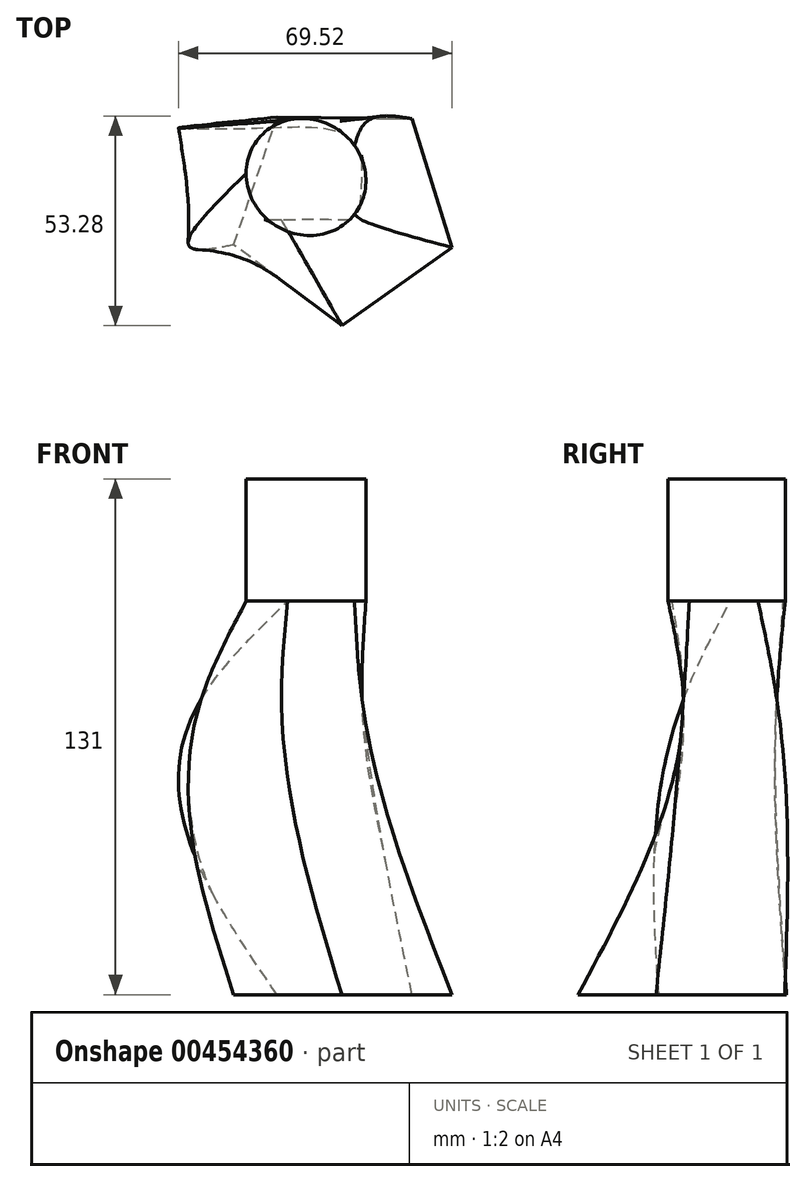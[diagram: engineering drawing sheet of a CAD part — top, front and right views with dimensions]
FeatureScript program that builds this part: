
annotation { "Feature Type Name" : "Feature", "Feature Type Description" : "" }
export const myFeature = defineFeature(function(context is Context, id is Id, definition is map)
    precondition{}
    {
        {
            var Q0;
            Q0=qCreatedBy(makeId("Top.planeOp"),FACE);
            var sketch = newSketch(context, id + "F0", { "sketchPlane" : qUnion([Q0])});
            skCircle(sketch, "E0.cCircle", {"center": v(0, 0) * mm, "radius": 23.6 * mm, "construction": true});
            skLineSegment(sketch, "E0.0", {"start": v(27.62, -9.36) * mm, "end": v(-0.36, -29.16) * mm});
            skLineSegment(sketch, "E0.1", {"start": v(-0.36, -29.16) * mm, "end": v(-27.85, -8.67) * mm});
            skLineSegment(sketch, "E0.2", {"start": v(-27.85, -8.67) * mm, "end": v(-16.85, 23.8) * mm});
            skLineSegment(sketch, "E0.3", {"start": v(-16.85, 23.8) * mm, "end": v(17.44, 23.38) * mm});
            skLineSegment(sketch, "E0.4", {"start": v(17.44, 23.38) * mm, "end": v(27.62, -9.36) * mm});
            skPoint(sketch, "E0.0.midPoint", {"position": v(13.63, -19.26) * mm});
            skSolve(sketch);
        }
        {
            var Q0;
            Q0=qCreatedBy(makeId("Top.planeOp"),FACE);
            cPlane(context, id + "F1", {"entities" : qUnion([Q0]), "cplaneType" : CPlaneType.OFFSET, "offset" : 75 * mm, "width" : 150 * mm, "height" : 150 * mm});
        }
        {
            var Q0;
            Q0=qCreatedBy(id+"F1.planeOp",FACE);
            var sketch = newSketch(context, id + "F2", { "sketchPlane" : qUnion([Q0])});
            skLineSegment(sketch, "E1.bottom", {"start": v(4.74, -2.37) * mm, "end": v(-36.15, -2.37) * mm});
            skLineSegment(sketch, "E1.top", {"start": v(4.74, 21.33) * mm, "end": v(-36.15, 21.33) * mm});
            skLineSegment(sketch, "E1.left", {"start": v(4.74, -2.37) * mm, "end": v(4.74, 21.33) * mm});
            skLineSegment(sketch, "E1.right", {"start": v(-36.15, -2.37) * mm, "end": v(-36.15, 21.33) * mm});
            skPoint(sketch, "E1.middle", {"position": v(-15.7, 9.48) * mm});
            skSolve(sketch);
        }
        {
            var Q0;
            Q0=qCreatedBy(id+"F1.planeOp",FACE);
            cPlane(context, id + "F3", {"entities" : qUnion([Q0]), "cplaneType" : CPlaneType.OFFSET, "offset" : 25 * mm, "width" : 150 * mm, "height" : 150 * mm});
        }
        {
            var Q0;
            Q0=qCreatedBy(id+"F3.planeOp",FACE);
            var sketch = newSketch(context, id + "F4", { "sketchPlane" : qUnion([Q0])});
            skEllipse(sketch, "E2", {"center": v(-9.48, 8.6) * mm, "majorRadius": 15.54 * mm, "minorRadius": 14.55 * mm, "majorAxis": v(0.82, -0.57)});
            skSolve(sketch);
        }
        {
            var Q0;
            Q0=makeQuery(id+"F0.imprint","IMPRINT",FACE,{"disambiguationData":[TD([[makeQuery(id+"F0.imprint","IMPRINT",EDGE,{"derivedFrom":sQuery(id+"F0.wireOp",EDGE,"E0.0")}),-1.0]])]});
            var Q1;
            Q1=makeQuery(id+"F2.imprint","IMPRINT",FACE,{"disambiguationData":[TD([[makeQuery(id+"F2.imprint","IMPRINT",EDGE,{"derivedFrom":sQuery(id+"F2.wireOp",EDGE,"E1.bottom")}),-1.0]])]});
            var Q2;
            Q2=makeQuery(id+"F4.imprint","IMPRINT",FACE,{"disambiguationData":[TD([[makeQuery(id+"F4.imprint","IMPRINT",EDGE,{"derivedFrom":sQuery(id+"F4.wireOp",EDGE,"E2")}),1.0]])]});
            loft(context, id + "F5", {"sheetProfilesArray" : [{ "sheetProfileEntities" : qUnion([Q0]) }, { "sheetProfileEntities" : qUnion([Q1]) }, { "sheetProfileEntities" : qUnion([Q2]) }]});
        }
        {
            var Q0;
            Q0=makeQuery(id+"F5.opLoft","CAP_FACE",FACE,{"disambiguationData":[OSD([makeQuery(id+"F4.imprint","IMPRINT",FACE,{"disambiguationData":[TD([[makeQuery(id+"F4.imprint","IMPRINT",EDGE,{"derivedFrom":sQuery(id+"F4.wireOp",EDGE,"E2")}),1.0]])]})])],"isStart":true});
            extrude(context, id + "F6", {"entities" : qUnion([Q0]), "operationType" : NewBodyOperationType.ADD, "depth" : 31 * mm});
        }
        {
            var Q0;
            Q0=qCreatedBy(makeId("Front.planeOp"),FACE);
            var sketch = newSketch(context, id + "F7", { "sketchPlane" : qUnion([Q0])});
            skCircle(sketch, "E3", {"center": v(-8.64, 116.2) * mm, "radius": 2.35 * mm});
            skSolve(sketch);
        }
        {
            var Q0;
            Q0=sQuery(id+"F7.wireOp",EDGE,"E3");
            extrude(context, id + "F8", {"bodyType" : ToolBodyType.SURFACE, "surfaceEntities" : qUnion([Q0]), "depth" : 17.3 * mm});
        }
    });
